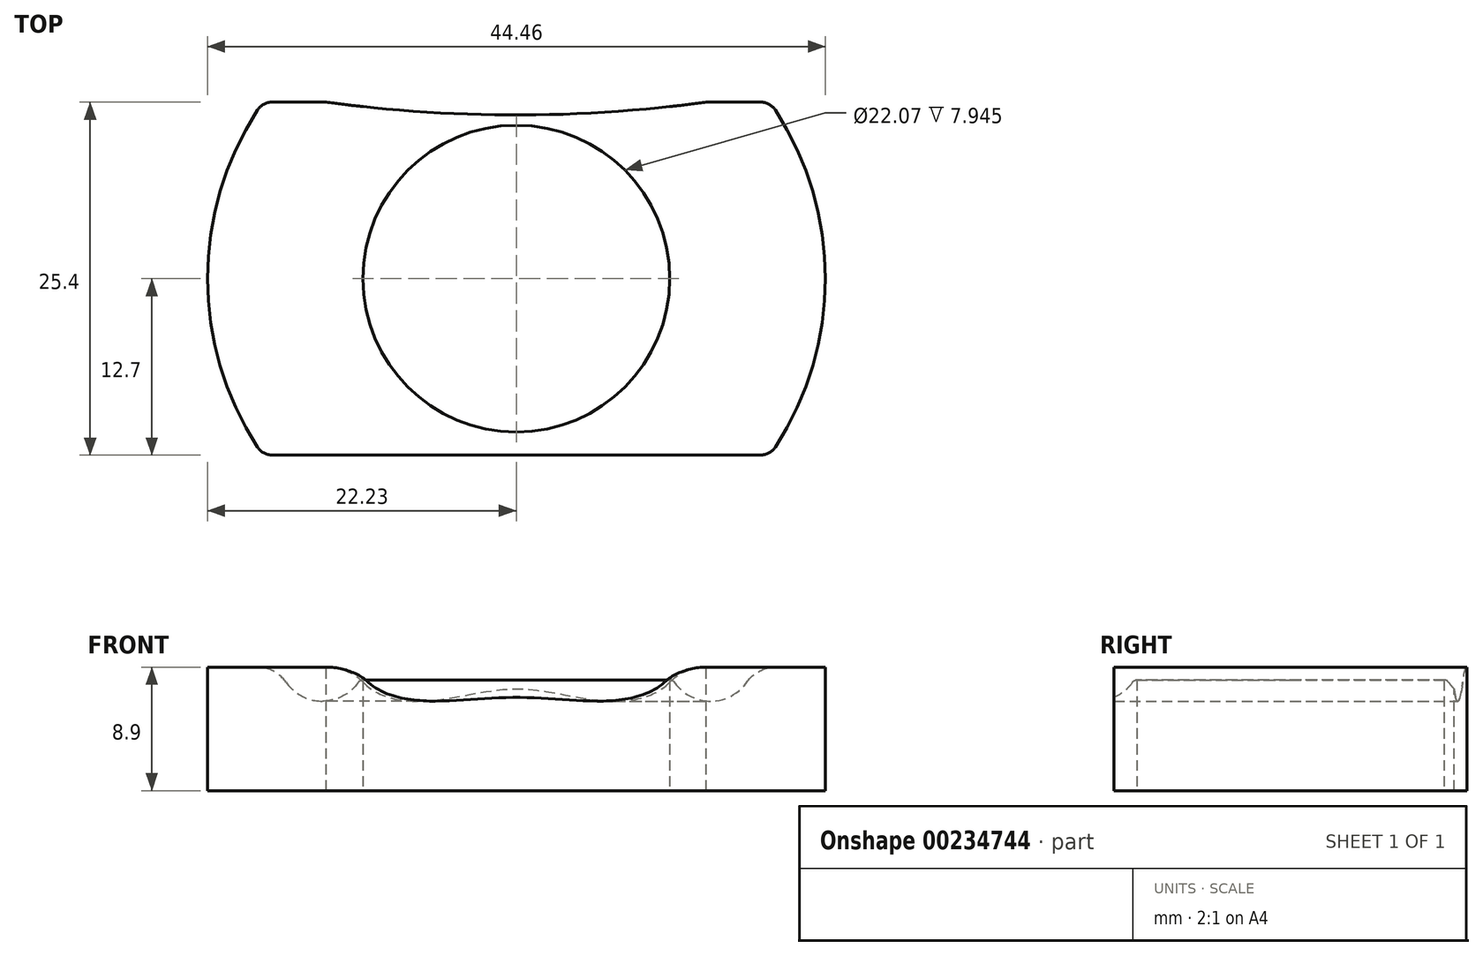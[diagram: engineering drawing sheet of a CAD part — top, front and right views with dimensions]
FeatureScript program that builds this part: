
annotation { "Feature Type Name" : "Feature", "Feature Type Description" : "" }
export const myFeature = defineFeature(function(context is Context, id is Id, definition is map)
    precondition{}
    {
        {
            var Q0;
            Q0=qCreatedBy(makeId("Top.planeOp"),FACE);
            var sketch = newSketch(context, id + "F0", { "sketchPlane" : qUnion([Q0])});
            skArc(sketch, "E0", {"start": v(-18.24, 12.7) * mm, "mid": v(-22.23, 0) * mm, "end": v(-18.24, -12.7) * mm});
            skLineSegment(sketch, "E1.bottom", {"start": v(18.24, 12.7) * mm, "end": v(-18.24, 12.7) * mm});
            skLineSegment(sketch, "E1.top", {"start": v(18.24, -12.7) * mm, "end": v(-18.24, -12.7) * mm});
            skLineSegment(sketch, "E1.left", {"start": v(18.24, 12.7) * mm, "end": v(18.24, -12.7) * mm, "construction": true});
            skLineSegment(sketch, "E1.right", {"start": v(-18.24, 12.7) * mm, "end": v(-18.24, -12.7) * mm, "construction": true});
            skArc(sketch, "E2.trimOffspring", {"start": v(18.24, -12.7) * mm, "mid": v(22.23, 0) * mm, "end": v(18.24, 12.7) * mm});
            skCircle(sketch, "E3", {"center": v(0, 0) * mm, "radius": 11.04 * mm});
            skSolve(sketch);
        }
        {
            var Q0;
            Q0=qSketchRegion(id+"F0",true);
            extrude(context, id + "F1", {"entities" : qUnion([Q0]), "endBound" : BoundingType.SYMMETRIC, "depth" : 8.9 * mm});
        }
        {
            var Q0;
            Q0=qCreatedBy(makeId("Front.planeOp"),FACE);
            var sketch = newSketch(context, id + "F2", { "sketchPlane" : qUnion([Q0])});
            skCircle(sketch, "E4", {"center": v(13.97, 5.18) * mm, "radius": 3.18 * mm});
            skLineSegment(sketch, "E5", {"start": v(13.97, 5.18) * mm, "end": v(13.97, 4.45) * mm});
            skLineSegment(sketch, "E6", {"start": v(13.97, 4.45) * mm, "end": v(13.97, 2) * mm});
            skLineSegment(sketch, "E7", {"start": v(12.88, 8.16) * mm, "end": v(0, 8.16) * mm});
            skLineSegment(sketch, "E8", {"start": v(0, 8.16) * mm, "end": v(0, 3.5) * mm});
            skLineSegment(sketch, "E9", {"start": v(0, 3.5) * mm, "end": v(16.67, 3.5) * mm});
            skLineSegment(sketch, "E10", {"start": v(0, 0) * mm, "end": v(-5.27, 0) * mm, "construction": true});
            skSolve(sketch);
        }
        {
            var Q0;
            Q0=qSketchRegion(id+"F2",true);
            var Q1;
            Q1=makeQuery(id+"F1.opExtrude","SWEPT_FACE",FACE,{"disambiguationData":[OSD([sQuery(id+"F0.wireOp",EDGE,"E3")])]});
            revolve(context, id + "F3", {"operationType" : NewBodyOperationType.REMOVE, "entities" : qUnion([Q0]), "axis" : qUnion([Q1]), "revolveType" : RevolveType.FULL, "oppositeDirection" : true});
        }
        {
            var Q0;
            Q0=makeQuery(id+"F3.boolean.opBoolean","INTERSECT",EDGE,{"disambiguationData":[OD(1.0)],"derivedFrom":[makeQuery(id+"F1.opExtrude","CAP_FACE",FACE,{"disambiguationData":[OSD([sQuery(id+"F0.wireOp",EDGE,"E0"),sQuery(id+"F0.wireOp",EDGE,"E1.bottom"),sQuery(id+"F0.wireOp",EDGE,"E1.top"),sQuery(id+"F0.wireOp",EDGE,"E2.trimOffspring"),sQuery(id+"F0.wireOp",EDGE,"E3")])],"isStart":false}),makeQuery(id+"F3.opRevolve","SWEPT_FACE",FACE,{"disambiguationData":[OSD([sQuery(id+"F2.wireOp",EDGE,"E4")])]})]});
            var Q1;
            Q1=makeQuery(id+"F3.boolean.opBoolean","INTERSECT",EDGE,{"disambiguationData":[OD(0.0)],"derivedFrom":[makeQuery(id+"F1.opExtrude","CAP_FACE",FACE,{"disambiguationData":[OSD([sQuery(id+"F0.wireOp",EDGE,"E0"),sQuery(id+"F0.wireOp",EDGE,"E1.bottom"),sQuery(id+"F0.wireOp",EDGE,"E1.top"),sQuery(id+"F0.wireOp",EDGE,"E2.trimOffspring"),sQuery(id+"F0.wireOp",EDGE,"E3")])],"isStart":false}),makeQuery(id+"F3.opRevolve","SWEPT_FACE",FACE,{"disambiguationData":[OSD([sQuery(id+"F2.wireOp",EDGE,"E4")])]})]});
            var Q2;
            Q2=makeQuery(id+"FBVG78wqvWEtJCH_1.1.F3.boolean.opBoolean","INTERSECT",EDGE,{"disambiguationData":[OD(1.0)],"derivedFrom":[makeQuery(id+"F1.opExtrude","CAP_FACE",FACE,{"disambiguationData":[OSD([sQuery(id+"F0.wireOp",EDGE,"E0"),sQuery(id+"F0.wireOp",EDGE,"E1.bottom"),sQuery(id+"F0.wireOp",EDGE,"E1.top"),sQuery(id+"F0.wireOp",EDGE,"E2.trimOffspring"),sQuery(id+"F0.wireOp",EDGE,"E3")])],"isStart":true}),makeQuery(id+"FBVG78wqvWEtJCH_1.1.F3.opRevolve","SWEPT_FACE",FACE,{"disambiguationData":[OSD([sQuery(id+"F2.wireOp",EDGE,"E4")])]})]});
            var Q3;
            Q3=makeQuery(id+"FBVG78wqvWEtJCH_1.1.F3.boolean.opBoolean","INTERSECT",EDGE,{"disambiguationData":[OD(0.0)],"derivedFrom":[makeQuery(id+"F1.opExtrude","CAP_FACE",FACE,{"disambiguationData":[OSD([sQuery(id+"F0.wireOp",EDGE,"E0"),sQuery(id+"F0.wireOp",EDGE,"E1.bottom"),sQuery(id+"F0.wireOp",EDGE,"E1.top"),sQuery(id+"F0.wireOp",EDGE,"E2.trimOffspring"),sQuery(id+"F0.wireOp",EDGE,"E3")])],"isStart":true}),makeQuery(id+"FBVG78wqvWEtJCH_1.1.F3.opRevolve","SWEPT_FACE",FACE,{"disambiguationData":[OSD([sQuery(id+"F2.wireOp",EDGE,"E4")])]})]});
            fillet(context, id + "F4", {"entities" : qUnion([Q0, Q1, Q2, Q3]), "radius" : 2.54 * mm, "tangentPropagation" : true, "allowEdgeOverflow" : false});
        }
        {
            var Q0;
            Q0=makeQuery(id+"F3.boolean.opBoolean","COPY",EDGE,{"derivedFrom":makeQuery(id+"F3.opRevolve","SWEPT_EDGE",EDGE,{"disambiguationData":[OSD([sQuery(id+"F2.wireOp",EDGE,"E4"),sQuery(id+"F2.wireOp",EDGE,"E9")])]})});
            var Q1;
            Q1=makeQuery(id+"FBVG78wqvWEtJCH_1.1.F3.boolean.opBoolean","COPY",EDGE,{"derivedFrom":makeQuery(id+"FBVG78wqvWEtJCH_1.1.F3.opRevolve","SWEPT_EDGE",EDGE,{"disambiguationData":[OSD([sQuery(id+"F2.wireOp",EDGE,"E4"),sQuery(id+"F2.wireOp",EDGE,"E9")])]})});
            fillet(context, id + "F5", {"entities" : qUnion([Q0, Q1]), "radius" : 0.25 * mm, "tangentPropagation" : true, "allowEdgeOverflow" : false});
        }
        {
            var Q0;
            Q0=makeQuery(id+"F1.opExtrude","SWEPT_EDGE",EDGE,{"disambiguationData":[OSD([sQuery(id+"F0.wireOp",EDGE,"E0"),sQuery(id+"F0.wireOp",EDGE,"E1.top")])]});
            var Q1;
            Q1=makeQuery(id+"F1.opExtrude","SWEPT_EDGE",EDGE,{"disambiguationData":[OSD([sQuery(id+"F0.wireOp",EDGE,"E1.top"),sQuery(id+"F0.wireOp",EDGE,"E2.trimOffspring")])]});
            var Q2;
            Q2=makeQuery(id+"F1.opExtrude","SWEPT_EDGE",EDGE,{"disambiguationData":[OSD([sQuery(id+"F0.wireOp",EDGE,"E0"),sQuery(id+"F0.wireOp",EDGE,"E1.bottom")])]});
            var Q3;
            Q3=makeQuery(id+"F1.opExtrude","SWEPT_EDGE",EDGE,{"disambiguationData":[OSD([sQuery(id+"F0.wireOp",EDGE,"E1.bottom"),sQuery(id+"F0.wireOp",EDGE,"E2.trimOffspring")])]});
            fillet(context, id + "F6", {"entities" : qUnion([Q0, Q1, Q2, Q3]), "radius" : 1.27 * mm, "tangentPropagation" : true, "allowEdgeOverflow" : false});
        }
        {
            var Q0;
            Q0=qCreatedBy(makeId("Top.planeOp"),FACE);
            var sketch = newSketch(context, id + "F7", { "sketchPlane" : qUnion([Q0])});
            skArc(sketch, "E11", {"start": v(-13.67, 12.7) * mm, "mid": v(0, 11.78) * mm, "end": v(13.67, 12.7) * mm});
            skLineSegment(sketch, "E12", {"start": v(-13.67, 12.7) * mm, "end": v(-13.67, 17.97) * mm});
            skLineSegment(sketch, "E13", {"start": v(-13.67, 17.97) * mm, "end": v(13.67, 17.97) * mm});
            skLineSegment(sketch, "E14", {"start": v(13.67, 17.97) * mm, "end": v(13.67, 12.7) * mm});
            skSolve(sketch);
        }
        {
            var Q0;
            Q0 = qSketchRegion(id + "F7", true);
            extrude(context, id + "F8", {"entities" : qUnion([Q0]), "operationType" : NewBodyOperationType.REMOVE, "endBound" : BoundingType.THROUGH_ALL, "oppositeDirection" : true, "depth" : 25.4 * mm, "hasSecondDirection" : true, "secondDirectionBound" : SecondDirectionBoundingType.THROUGH_ALL, "secondDirectionOppositeDirection" : false, "secondDirectionDepth" : 25.4 * mm});
        }
    });
